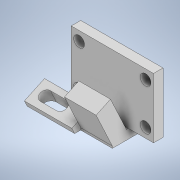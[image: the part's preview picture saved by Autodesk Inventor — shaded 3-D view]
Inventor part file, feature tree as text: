
AUTODESK INVENTOR PART (.ipt)
format: ipt  version: 2022.6 (Build 266554000, 554)  size: 177,152 bytes
history: native  units: mm
features: sketch x5, extrude x4, hole x1, projected_geometry x1
ambient origin geometry x8: Origin, YZ Plane, XZ Plane, XY Plane, X Axis, Y Axis, Z Axis, Center Point
bodies: Solid1 (feature_tree)
feature tree (11):
  extrude  "Extrusion1"  Depth=13.0mm
  hole  "Hole1"  [1 undecoded]
  extrude  "Extrusion2"  Depth=3.0mm
  extrude  "Extrusion3"  Depth=3.4mm
  extrude  "Extrusion5"  Depth=3.4mm
  sketch  "Sketch1"  dims[d0=21.0mm d1=13.0mm]
  sketch  "Sketch2"  dims[d2=26.0mm d3=19.0mm]
  sketch  "Sketch3"  dims[d4=3.0mm d5=0.0mm]
  projected_geometry  "Projected Loop1"
  sketch  "Sketch4"  dims[d6=3.4mm d7=6.0mm d8=4.0mm d9=2.0mm d10=90.0deg d11=8.0mm d12=20.594885mm d13=3.0mm]
  sketch  "Sketch6"  dims[d14=8.0mm d15=4.363323mm d16=4.0mm d17=10.0mm d18=10.0mm d19=0.0mm d20=1.0mm d21=2.144507mm d23=15.0mm d24=0.0mm d25=3.0mm d33=2.0mm d34=5.0mm d35=3.4mm d36=6.0mm d37=0.0mm d38=0.0mm]
note: 1 required parameter value undecoded (feature->parameter linkage not recoverable at this tier; creation-order binding heuristic only, values carry confidence <= 0.55)
